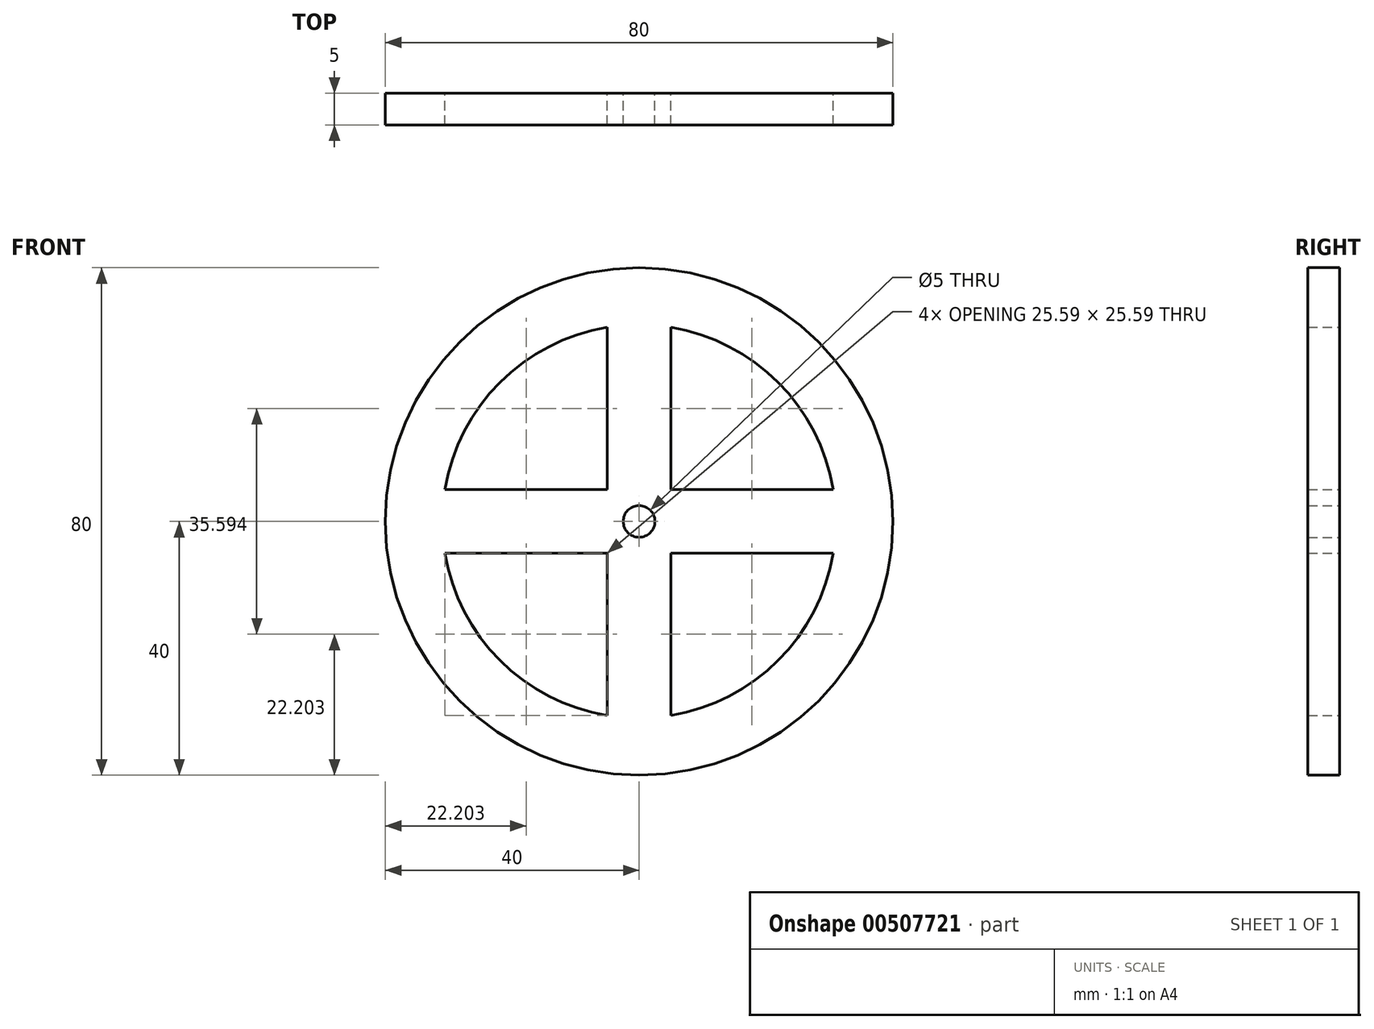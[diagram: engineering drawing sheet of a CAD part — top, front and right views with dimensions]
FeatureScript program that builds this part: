
annotation { "Feature Type Name" : "Feature", "Feature Type Description" : "" }
export const myFeature = defineFeature(function(context is Context, id is Id, definition is map)
    precondition{}
    {
        {
            var Q0;
            Q0=qCreatedBy(makeId("Front.planeOp"),FACE);
            var sketch = newSketch(context, id + "F0", { "sketchPlane" : qUnion([Q0])});
            skCircle(sketch, "E0", {"center": v(0, 0) * mm, "radius": 40 * mm});
            skArc(sketch, "E1", {"start": v(-5, 30.6) * mm, "mid": v(-21.92, 21.92) * mm, "end": v(-30.6, 5) * mm});
            skArc(sketch, "E2", {"start": v(5, -5.6) * mm, "mid": v(5.3, -5.3) * mm, "end": v(5.6, -5) * mm});
            skCircle(sketch, "E3", {"center": v(0, 0) * mm, "radius": 2.5 * mm});
            skLineSegment(sketch, "E4", {"start": v(0, 0) * mm, "end": v(0, 31) * mm, "construction": true});
            skLineSegment(sketch, "E5", {"start": v(0, 0) * mm, "end": v(2.5, 0) * mm});
            skLineSegment(sketch, "E6", {"start": v(0, 0) * mm, "end": v(0, -31) * mm, "construction": true});
            skLineSegment(sketch, "E7", {"start": v(0, 0) * mm, "end": v(-2.5, 0) * mm});
            skLineSegment(sketch, "E8.0", {"start": v(-5, 5) * mm, "end": v(-5, 30.6) * mm});
            skLineSegment(sketch, "E9.0", {"start": v(5, 5) * mm, "end": v(5, 30.6) * mm});
            skLineSegment(sketch, "E10.0", {"start": v(-5, 5) * mm, "end": v(-30.6, 5) * mm});
            skLineSegment(sketch, "E11.0", {"start": v(-5, -5) * mm, "end": v(-30.6, -5) * mm});
            skLineSegment(sketch, "E12.0", {"start": v(-5, -5) * mm, "end": v(-5, -30.6) * mm});
            skLineSegment(sketch, "E13.0", {"start": v(5, -5) * mm, "end": v(5, -30.6) * mm});
            skLineSegment(sketch, "E14.0", {"start": v(0, 0) * mm, "end": v(-31, 0) * mm, "construction": true});
            skLineSegment(sketch, "E15.0", {"start": v(5, 5) * mm, "end": v(30.6, 5) * mm});
            skLineSegment(sketch, "E16.0", {"start": v(5, -5) * mm, "end": v(30.6, -5) * mm});
            skArc(sketch, "E17.trimOffspring", {"start": v(-30.6, -5) * mm, "mid": v(-21.92, -21.92) * mm, "end": v(-5, -30.6) * mm});
            skArc(sketch, "E18.trimOffspring", {"start": v(5, -30.6) * mm, "mid": v(21.92, -21.92) * mm, "end": v(30.6, -5) * mm});
            skArc(sketch, "E19.trimOffspring", {"start": v(30.6, 5) * mm, "mid": v(21.92, 21.92) * mm, "end": v(5, 30.6) * mm});
            skArc(sketch, "E20.trimOffspring", {"start": v(5.6, 5) * mm, "mid": v(5.3, 5.3) * mm, "end": v(5, 5.6) * mm});
            skArc(sketch, "E21.trimOffspring", {"start": v(-5, 5.6) * mm, "mid": v(-5.3, 5.3) * mm, "end": v(-5.6, 5) * mm});
            skArc(sketch, "E22.trimOffspring", {"start": v(-5.6, -5) * mm, "mid": v(-5.3, -5.3) * mm, "end": v(-5, -5.6) * mm});
            skLineSegment(sketch, "E23.trimOffspring", {"start": v(5, 0) * mm, "end": v(31, 0) * mm, "construction": true});
            skLineSegment(sketch, "E24.trimOffspring", {"start": v(-5, 0) * mm, "end": v(-31, 0) * mm});
            skSolve(sketch);
        }
        {
            var Q0;
            Q0=makeQuery(id+"F0.imprint","IMPRINT",FACE,{"disambiguationData":[TD([[makeQuery(id+"F0.imprint","IMPRINT",EDGE,{"derivedFrom":sQuery(id+"F0.wireOp",EDGE,"E0")}),1.0]])]});
            extrude(context, id + "F1", {"entities" : qUnion([Q0]), "endBound" : BoundingType.SYMMETRIC, "depth" : 5 * mm});
        }
    });
